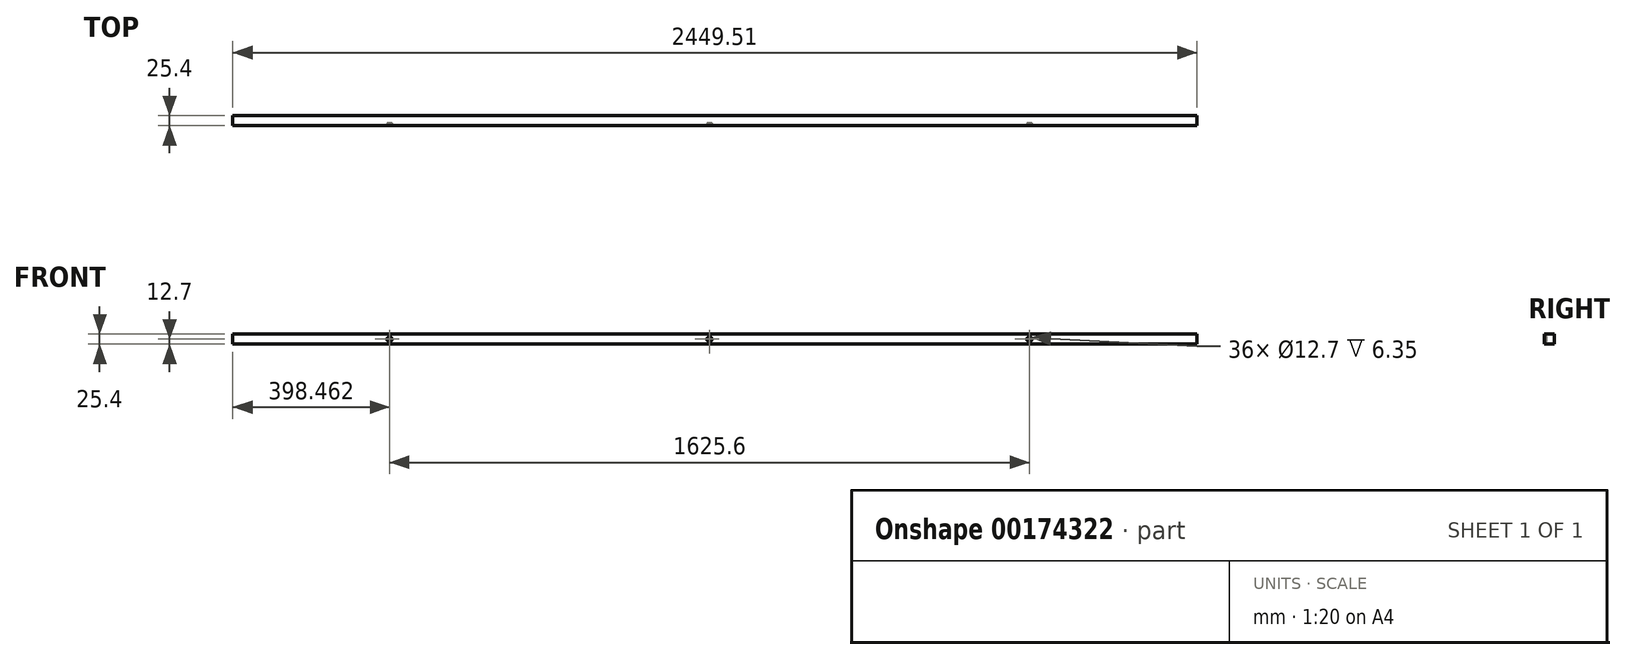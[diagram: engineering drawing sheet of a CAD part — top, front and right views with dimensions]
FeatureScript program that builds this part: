
annotation { "Feature Type Name" : "Feature", "Feature Type Description" : "" }
export const myFeature = defineFeature(function(context is Context, id is Id, definition is map)
    precondition{}
    {
        {
            var Q0;
            Q0=qCreatedBy(makeId("Front.planeOp"),FACE);
            var sketch = newSketch(context, id + "F0", { "sketchPlane" : qUnion([Q0])});
            skLineSegment(sketch, "E0.bottom", {"start": v(0, 0) * mm, "end": v(2449.51, 0) * mm});
            skLineSegment(sketch, "E0.top", {"start": v(0, 25.4) * mm, "end": v(2449.51, 25.4) * mm});
            skLineSegment(sketch, "E0.left", {"start": v(0, 0) * mm, "end": v(0, 25.4) * mm});
            skLineSegment(sketch, "E0.right", {"start": v(2449.51, 0) * mm, "end": v(2449.51, 25.4) * mm});
            skSolve(sketch);
        }
        {
            var Q0;
            Q0=makeQuery(id+"F0.imprint","IMPRINT",FACE,{"disambiguationData":[TD([[makeQuery(id+"F0.imprint","IMPRINT",EDGE,{"derivedFrom":sQuery(id+"F0.wireOp",EDGE,"E0.bottom")}),1.0]])]});
            extrude(context, id + "F1", {"entities" : qUnion([Q0]), "depth" : 25.4 * mm});
        }
        {
            var Q0;
            Q0=makeQuery(id+"F1.opExtrude","CAP_FACE",FACE,{"disambiguationData":[OSD([sQuery(id+"F0.wireOp",EDGE,"E0.bottom"),sQuery(id+"F0.wireOp",EDGE,"E0.top"),sQuery(id+"F0.wireOp",EDGE,"E0.left"),sQuery(id+"F0.wireOp",EDGE,"E0.right")])],"isStart":false});
            var sketch = newSketch(context, id + "F2", { "sketchPlane" : qUnion([Q0])});
            skCircle(sketch, "E1", {"center": v(2024.06, 12.7) * mm, "radius": 6.35 * mm});
            skCircle(sketch, "E2", {"center": v(1211.26, 12.7) * mm, "radius": 6.35 * mm});
            skCircle(sketch, "E3", {"center": v(398.46, 12.7) * mm, "radius": 6.35 * mm});
            skSolve(sketch);
        }
        {
            var Q0;
            Q0 = qSketchRegion(id + "F2", true);
            extrude(context, id + "F3", {"entities" : qUnion([Q0]), "operationType" : NewBodyOperationType.REMOVE, "oppositeDirection" : true, "depth" : 6.35 * mm});
        }
    });
